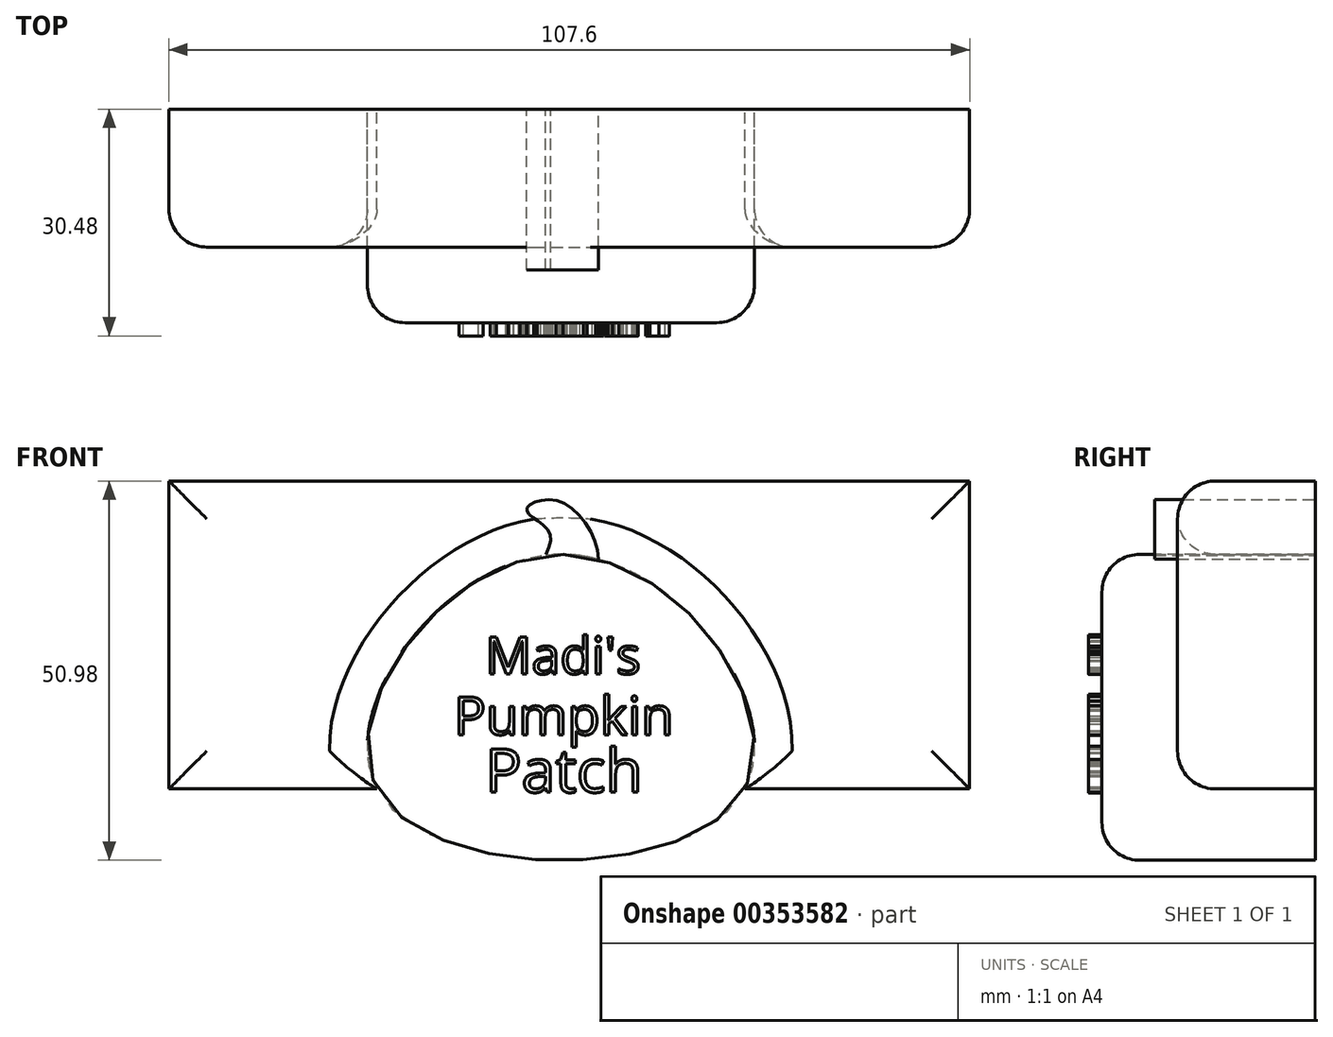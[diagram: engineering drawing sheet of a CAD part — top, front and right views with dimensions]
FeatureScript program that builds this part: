
annotation { "Feature Type Name" : "Feature", "Feature Type Description" : "" }
export const myFeature = defineFeature(function(context is Context, id is Id, definition is map)
    precondition{}
    {
        {
            var Q0;
            Q0=qCreatedBy(makeId("Front.planeOp"),FACE);
            var sketch = newSketch(context, id + "F0", { "sketchPlane" : qUnion([Q0])});
            skLineSegment(sketch, "E0.bottom", {"start": v(-53.01, 18.13) * mm, "end": v(54.59, 18.13) * mm});
            skLineSegment(sketch, "E0.top", {"start": v(-53.01, -23.25) * mm, "end": v(54.59, -23.25) * mm});
            skLineSegment(sketch, "E0.left", {"start": v(-53.01, 18.13) * mm, "end": v(-53.01, -23.25) * mm});
            skLineSegment(sketch, "E0.right", {"start": v(54.59, 18.13) * mm, "end": v(54.59, -23.25) * mm});
            skSolve(sketch);
        }
        {
            var Q0;
            Q0=makeQuery(id+"F0.imprint","IMPRINT",FACE,{"disambiguationData":[TD([[makeQuery(id+"F0.imprint","IMPRINT",EDGE,{"derivedFrom":sQuery(id+"F0.wireOp",EDGE,"E0.bottom")}),-1.0]])]});
            var sketch = newSketch(context, id + "F1", { "sketchPlane" : qUnion([Q0])});
            skFitSpline(sketch, "E1", {"points": [v(0, 8.28) * mm, v(-24.83, -23.65) * mm, v(24.04, -23.85) * mm, v(0, 8.28) * mm]});
            skSolve(sketch);
        }
        {
            var Q0;
            {var subQ0=sQuery(id+"F1.wireOp",EDGE,"E1");var subQ1=makeQuery(id+"F0.imprint","IMPRINT",EDGE,{"derivedFrom":sQuery(id+"F0.wireOp",EDGE,"E0.top")});var subQ2=makeQuery(id+"F1.imprint","INTERSECT",VERTEX,{"disambiguationData":[OD(0.0)],"derivedFrom":[subQ1,subQ0]});Q0=makeQuery(id+"F1.imprint","IMPRINT",FACE,{"disambiguationData":[TD([[makeQuery(id+"F1.imprint","IMPRINT",EDGE,{"disambiguationData":[TD([[subQ2,1.0]])],"derivedFrom":subQ0}),1.0]])]});}
            var sketch = newSketch(context, id + "F2", { "sketchPlane" : qUnion([Q0])});
            skFitSpline(sketch, "E2", {"points": [v(3.94, 5.12) * mm, v(0, 15.17) * mm, v(-4.93, 14.19) * mm, v(-1.77, 10.84) * mm, v(-4.73, 4.73) * mm, v(-4.73, 4.34) * mm, v(3.94, 5.12) * mm]});
            skSolve(sketch);
        }
        {
            var Q0;
            Q0=makeQuery(id+"F1.imprint","IMPRINT",FACE,{"disambiguationData":[TD([[makeQuery(id+"F1.imprint","IMPRINT",EDGE,{"derivedFrom":makeQuery(id+"F0.imprint","IMPRINT",EDGE,{"derivedFrom":sQuery(id+"F0.wireOp",EDGE,"E0.bottom")})}),-1.0]])]});
            extrude(context, id + "F3", {"entities" : qUnion([Q0]), "depth" : 18.54 * mm});
        }
        {
            var Q0;
            {var subQ0=sQuery(id+"F2.wireOp",EDGE,"E2");var subQ1=sQuery(id+"F1.wireOp",EDGE,"E1");var subQ2=makeQuery(id+"F0.imprint","IMPRINT",EDGE,{"derivedFrom":sQuery(id+"F0.wireOp",EDGE,"E0.top")});var subQ3=makeQuery(id+"F1.imprint","IMPRINT",EDGE,{"disambiguationData":[TD([[makeQuery(id+"F1.imprint","INTERSECT",VERTEX,{"disambiguationData":[OD(0.0)],"derivedFrom":[subQ2,subQ1]}),1.0]])],"derivedFrom":subQ1});var subQ4=makeQuery(id+"F2.imprint","INTERSECT",VERTEX,{"disambiguationData":[OD(0.0)],"derivedFrom":[subQ3,subQ0]});Q0=makeQuery(id+"F2.imprint","IMPRINT",FACE,{"disambiguationData":[TD([[makeQuery(id+"F2.imprint","IMPRINT",EDGE,{"disambiguationData":[TD([[subQ4,1.0]])],"derivedFrom":subQ0}),1.0]])]});}
            var Q1;
            Q1=sQuery(id+"F2.wireOp",EDGE,"E2");
            extrude(context, id + "F4", {"entities" : qUnion([Q0]), "surfaceEntities" : qUnion([Q1]), "depth" : 21.59 * mm});
        }
        {
            var Q0;
            Q0 = qSketchRegion(id + "F1", true);
            extrude(context, id + "F5", {"entities" : qUnion([Q0]), "depth" : 28.7 * mm});
        }
        {
            var Q0;
            Q0=makeQuery(id+"F3.opExtrude","CAP_FACE",FACE,{"disambiguationData":[OSD([sQuery(id+"F0.wireOp",EDGE,"E0.bottom"),sQuery(id+"F0.wireOp",EDGE,"E0.top"),sQuery(id+"F0.wireOp",EDGE,"E0.left"),sQuery(id+"F0.wireOp",EDGE,"E0.right"),sQuery(id+"F1.wireOp",EDGE,"E1")])],"isStart":false});
            fillet(context, id + "F6", {"entities" : qUnion([Q0]), "radius" : 5.08 * mm, "tangentPropagation" : true, "allowEdgeOverflow" : false});
        }
        {
            var Q0;
            Q0=makeQuery(id+"F5.opExtrude","CAP_FACE",FACE,{"disambiguationData":[OSD([sQuery(id+"F1.wireOp",EDGE,"E1")])],"isStart":false});
            fillet(context, id + "F7", {"entities" : qUnion([Q0]), "radius" : 5.08 * mm, "tangentPropagation" : true, "allowEdgeOverflow" : false});
        }
        {
            var Q0;
            Q0=qCreatedBy(makeId("Front.planeOp"),FACE);
            var sketch = newSketch(context, id + "F8", { "sketchPlane" : qUnion([Q0])});
            skText(sketch, "E3", { "text": "Madi\'s", "fontName": "OpenSans-Regular.ttf"});
            skText(sketch, "E4", { "text": "Pumpkin", "fontName": "OpenSans-Regular.ttf"});
            skText(sketch, "E5", { "text": "Patch", "fontName": "OpenSans-Regular.ttf"});
            skPoint(sketch, "E5.firstSnap0", {"position": v(-10.52, -5.32) * mm});
            const initialGuessF8  = {"E3": [-0.01052, -0.0078, 1, 0, 0.00498], "E4": [-0.01471, -0.01596, 1, 0, 0.00512], "E5": [-0.01052, -0.0237, 1, 0, 0.00586]};
            skSetInitialGuess(sketch, initialGuessF8);
            skSolve(sketch);
        }
        {
            var Q0;
            Q0 = qSketchRegion(id + "F8", true);
            extrude(context, id + "F9", {"entities" : qUnion([Q0]), "operationType" : NewBodyOperationType.ADD, "depth" : 30.48 * mm});
        }
    });
